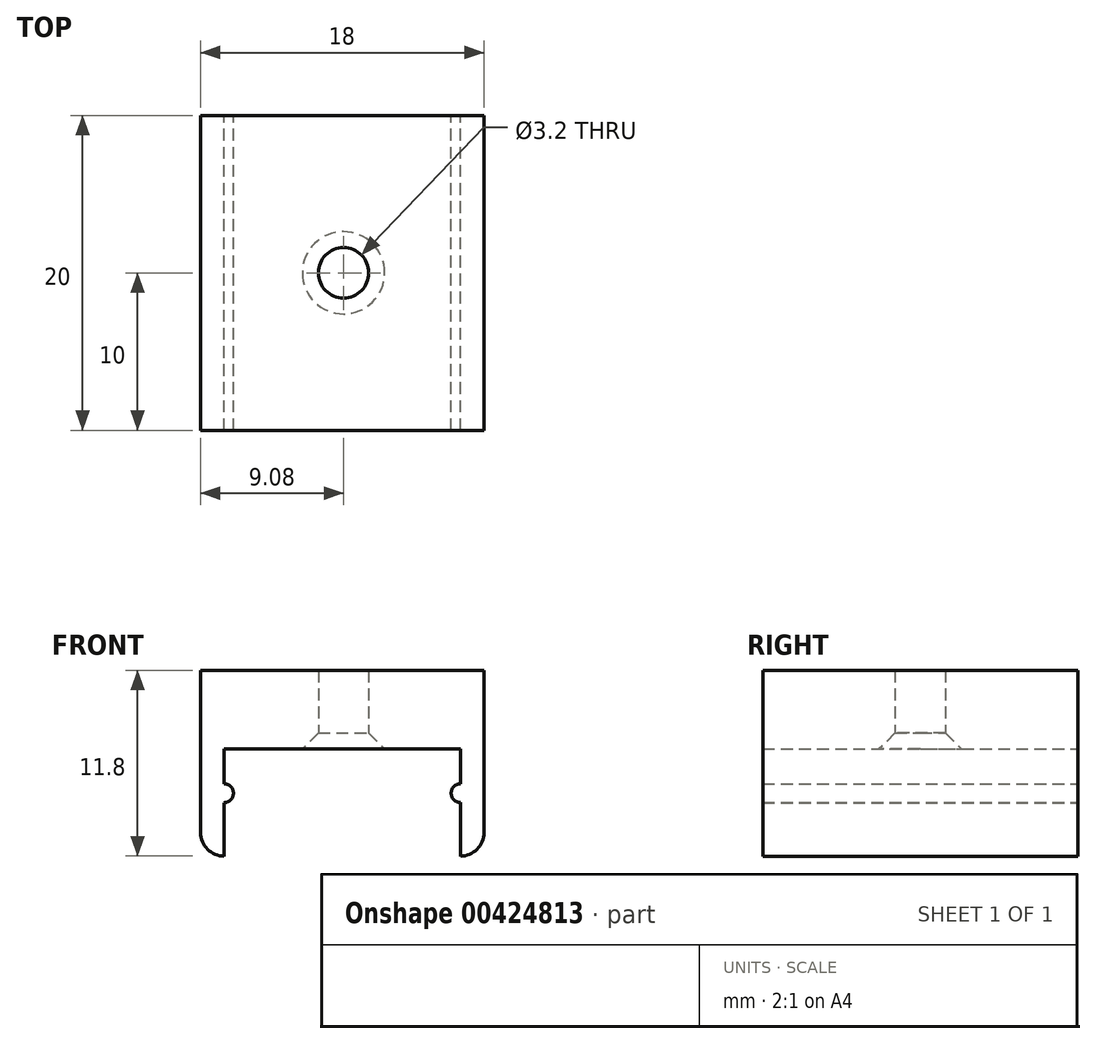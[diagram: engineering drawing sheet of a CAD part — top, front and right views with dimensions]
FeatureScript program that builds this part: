
annotation { "Feature Type Name" : "Feature", "Feature Type Description" : "" }
export const myFeature = defineFeature(function(context is Context, id is Id, definition is map)
    precondition{}
    {
        {
            var Q0;
            Q0=qCreatedBy(makeId("Front.planeOp"),FACE);
            var sketch = newSketch(context, id + "F0", { "sketchPlane" : qUnion([Q0])});
            skLineSegment(sketch, "E0.bottom", {"start": v(-3.59, 5.14) * mm, "end": v(14.41, 5.14) * mm});
            skLineSegment(sketch, "E0.top", {"start": v(-2.09, 0.14) * mm, "end": v(5.41, 0.14) * mm});
            skLineSegment(sketch, "E0.right", {"start": v(14.41, 5.14) * mm, "end": v(14.41, 0.14) * mm});
            skLineSegment(sketch, "E1.top", {"start": v(-2.13, -6.66) * mm, "end": v(-2.09, -6.66) * mm});
            skLineSegment(sketch, "E1.right", {"start": v(-2.09, 0.14) * mm, "end": v(-2.09, -6.66) * mm});
            skLineSegment(sketch, "E2.top", {"start": v(12.87, -6.66) * mm, "end": v(12.91, -6.66) * mm});
            skLineSegment(sketch, "E2.left", {"start": v(12.91, 0.14) * mm, "end": v(12.91, -6.66) * mm});
            skLineSegment(sketch, "E2.right", {"start": v(14.41, 0.14) * mm, "end": v(14.41, -0.62) * mm});
            skPoint(sketch, "E3", {"position": v(-2.09, -2.06) * mm});
            skArc(sketch, "E4", {"start": v(-2.09, -3.26) * mm, "mid": v(-1.5, -2.66) * mm, "end": v(-2.09, -2.06) * mm});
            skPoint(sketch, "E5", {"position": v(12.91, -3.26) * mm});
            skArc(sketch, "E6", {"start": v(12.91, -2.06) * mm, "mid": v(12.33, -2.66) * mm, "end": v(12.91, -3.26) * mm});
            skPoint(sketch, "E7.visualSharp", {"position": v(-3.59, -6.66) * mm});
            skPoint(sketch, "E8.visualSharp", {"position": v(14.41, -6.66) * mm});
            skPoint(sketch, "E9", {"position": v(5.41, 0.14) * mm});
            skLineSegment(sketch, "E10", {"start": v(-2.09, -6.66) * mm, "end": v(-2.13, -6.66) * mm});
            skPoint(sketch, "E0.left.end.orphan", {"position": v(-3.59, 0.14) * mm});
            skLineSegment(sketch, "E11", {"start": v(12.91, -6.66) * mm, "end": v(12.91, -6.66) * mm});
            skLineSegment(sketch, "E12", {"start": v(14.41, -0.62) * mm, "end": v(14.41, -5.16) * mm});
            skLineSegment(sketch, "E13", {"start": v(-2.09, -6.66) * mm, "end": v(-2.09, -6.66) * mm});
            skLineSegment(sketch, "E14", {"start": v(-3.59, -5.16) * mm, "end": v(-3.59, 0.14) * mm});
            skLineSegment(sketch, "E15", {"start": v(-3.59, 5.14) * mm, "end": v(-3.59, 0.14) * mm});
            skLineSegment(sketch, "E16", {"start": v(5.41, 0.14) * mm, "end": v(12.91, 0.14) * mm});
            skArc(sketch, "E17.filletArc", {"start": v(-3.59, -5.16) * mm, "mid": v(-3.15, -6.22) * mm, "end": v(-2.09, -6.66) * mm});
            skArc(sketch, "E18.filletArc", {"start": v(12.91, -6.66) * mm, "mid": v(13.97, -6.22) * mm, "end": v(14.41, -5.16) * mm});
            skSolve(sketch);
        }
        {
            var Q0;
            Q0=makeQuery(id+"F0.imprint","IMPRINT",FACE,{"disambiguationData":[TD([[makeQuery(id+"F0.imprint","IMPRINT",EDGE,{"derivedFrom":sQuery(id+"F0.wireOp",EDGE,"E0.bottom")}),-1.0]])]});
            extrude(context, id + "F1", {"entities" : qUnion([Q0]), "depth" : 20 * mm});
        }
        {
            var Q0;
            Q0=qCreatedBy(makeId("Top.planeOp"),FACE);
            var sketch = newSketch(context, id + "F2", { "sketchPlane" : qUnion([Q0])});
            skPoint(sketch, "E19", {"position": v(5.5, -10) * mm});
            skSolve(sketch);
        }
        {
            var Q0;
            Q0=sQuery(id+"F2.wireOp",VERTEX,"E19");
            var Q1;
            Q1=makeQuery(id+"F1.opExtrude","SWEPT_BODY",BODY,{"disambiguationData":[OSD([sQuery(id+"F0.wireOp",EDGE,"E0.bottom"),sQuery(id+"F0.wireOp",EDGE,"E0.top"),sQuery(id+"F0.wireOp",EDGE,"E0.right"),sQuery(id+"F0.wireOp",EDGE,"E1.right"),sQuery(id+"F0.wireOp",EDGE,"E2.left"),sQuery(id+"F0.wireOp",EDGE,"E2.right"),sQuery(id+"F0.wireOp",EDGE,"E12"),sQuery(id+"F0.wireOp",EDGE,"E14"),sQuery(id+"F0.wireOp",EDGE,"E15"),sQuery(id+"F0.wireOp",EDGE,"E16"),sQuery(id+"F0.wireOp",EDGE,"E17.filletArc"),sQuery(id+"F0.wireOp",EDGE,"E18.filletArc")])]});
            hole(context, id + "F3", {"style" : HoleStyle.C_SINK, "endStyle" : HoleEndStyle.THROUGH, "oppositeDirection" : true, "holeDiameter" : 3.2 * mm, "cSinkDiameter" : 5.5 * mm, "cSinkAngle" : 90 * degree, "isTappedThrough" : true, "tappedDepth" : 12 * mm, "tapClearance" : 3, "startFromSketch" : true, "locations" : qUnion([Q0]), "scope" : qUnion([Q1])});
        }
        {
            var Q0;
            {var subQ0=sQuery(id+"F0.wireOp",EDGE,"E4");Q0=makeQuery(id+"F0.imprint","IMPRINT",FACE,{"disambiguationData":[TD([[makeQuery(id+"F0.imprint","IMPRINT",EDGE,{"derivedFrom":subQ0}),1.0]])]});}
            var Q1;
            {var subQ0=sQuery(id+"F0.wireOp",EDGE,"E6");Q1=makeQuery(id+"F0.imprint","IMPRINT",FACE,{"disambiguationData":[TD([[makeQuery(id+"F0.imprint","IMPRINT",EDGE,{"derivedFrom":subQ0}),1.0]])]});}
            extrude(context, id + "F4", {"entities" : qUnion([Q0, Q1]), "operationType" : NewBodyOperationType.ADD, "depth" : 20 * mm});
        }
    });
